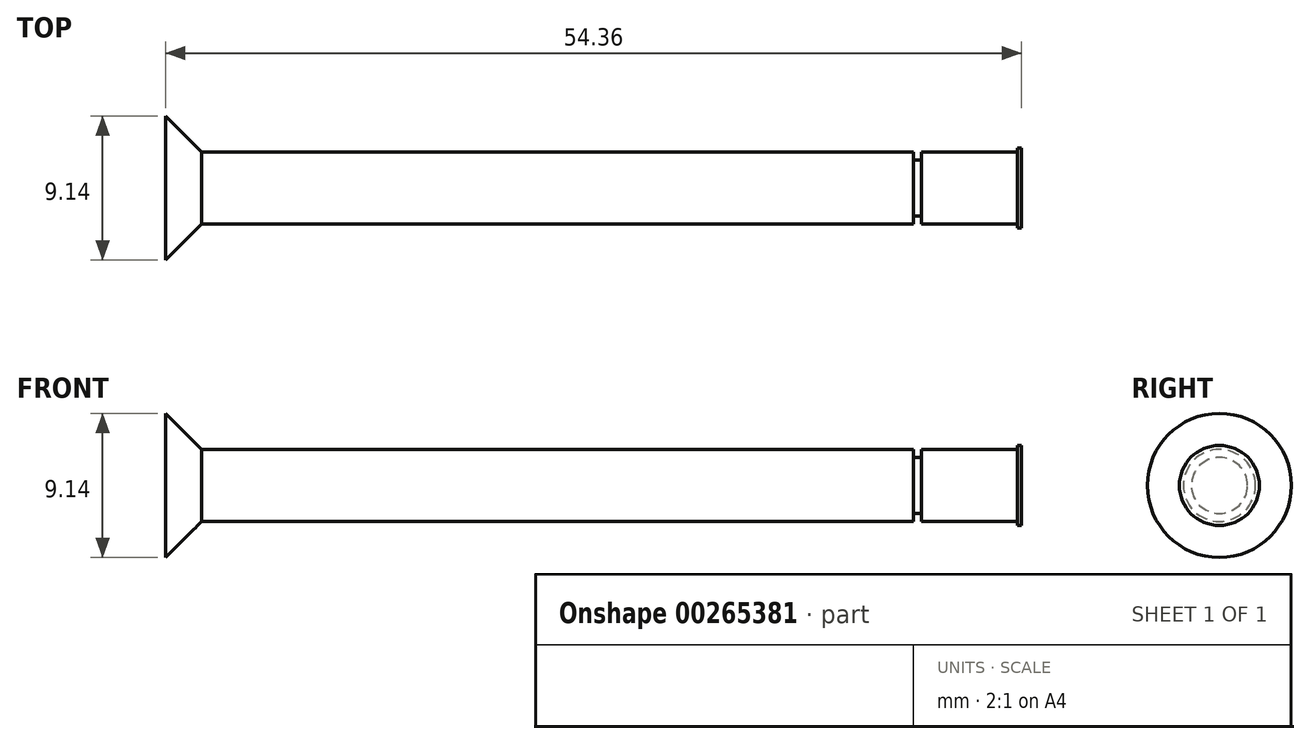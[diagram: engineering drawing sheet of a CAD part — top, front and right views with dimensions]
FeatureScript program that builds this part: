
annotation { "Feature Type Name" : "Feature", "Feature Type Description" : "" }
export const myFeature = defineFeature(function(context is Context, id is Id, definition is map)
    precondition{}
    {
        {
            var Q0;
            Q0=qCreatedBy(makeId("Front.planeOp"),FACE);
            var sketch = newSketch(context, id + "F0", { "sketchPlane" : qUnion([Q0])});
            skLineSegment(sketch, "E0", {"start": v(0, 0) * mm, "end": v(0, 4.57) * mm});
            skLineSegment(sketch, "E1", {"start": v(0, 4.57) * mm, "end": v(2.29, 2.29) * mm});
            skLineSegment(sketch, "E2", {"start": v(2.29, 2.29) * mm, "end": v(47.5, 2.29) * mm});
            skLineSegment(sketch, "E3", {"start": v(47.5, 2.29) * mm, "end": v(47.5, 1.78) * mm});
            skLineSegment(sketch, "E4", {"start": v(47.5, 1.78) * mm, "end": v(48, 1.78) * mm});
            skLineSegment(sketch, "E5", {"start": v(48, 1.78) * mm, "end": v(48, 2.29) * mm});
            skLineSegment(sketch, "E6", {"start": v(48, 2.29) * mm, "end": v(54.1, 2.29) * mm});
            skLineSegment(sketch, "E7", {"start": v(54.1, 2.29) * mm, "end": v(54.1, 2.54) * mm});
            skLineSegment(sketch, "E8", {"start": v(54.1, 2.54) * mm, "end": v(54.36, 2.54) * mm});
            skLineSegment(sketch, "E9", {"start": v(54.36, 2.54) * mm, "end": v(54.36, 0) * mm});
            skLineSegment(sketch, "E10", {"start": v(54.36, 0) * mm, "end": v(0, 0) * mm});
            skSolve(sketch);
        }
        {
            var Q0;
            Q0=makeQuery(id+"F0.imprint","IMPRINT",FACE,{"disambiguationData":[TD([[makeQuery(id+"F0.imprint","IMPRINT",EDGE,{"derivedFrom":sQuery(id+"F0.wireOp",EDGE,"E0")}),-1.0]])]});
            var Q1;
            Q1=sQuery(id+"F0.wireOp",EDGE,"E10");
            revolve(context, id + "F1", {"entities" : qUnion([Q0]), "axis" : qUnion([Q1]), "revolveType" : RevolveType.FULL});
        }
    });
